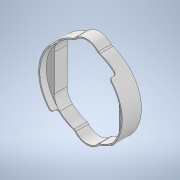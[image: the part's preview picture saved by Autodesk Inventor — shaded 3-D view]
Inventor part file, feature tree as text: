
AUTODESK INVENTOR PART (.ipt)
format: ipt  version: 2022 (Build 260153000, 153)  size: 123,904 bytes
history: native  units: in
note: dims shown in document units (in); Inventor stores cm internally (conversion verified against a paired STEP export)
features: other x3, sketch x1, plane x1, extrude x1, reference x1
ambient origin geometry x8: Origin, YZ Plane, XZ Plane, XY Plane, X Axis, Y Axis, Z Axis, Center Point
bodies: Solid1 (feature_tree)
feature tree (7):
  sketch  "Sketch1"  dims[d2=0.375in d3=0.0in d20=0.0157in d21=0.0394in]
  plane  "Work Plane1"
  extrude  "Extrusion1"  Depth=0.0157in
  reference  "Reference1"
  other  "<userpath>\Documents\CAD\guardSwerve1\Assembly1.iam"
  other  "Assembly1.iam"
  other  "Undercarriage:1"
